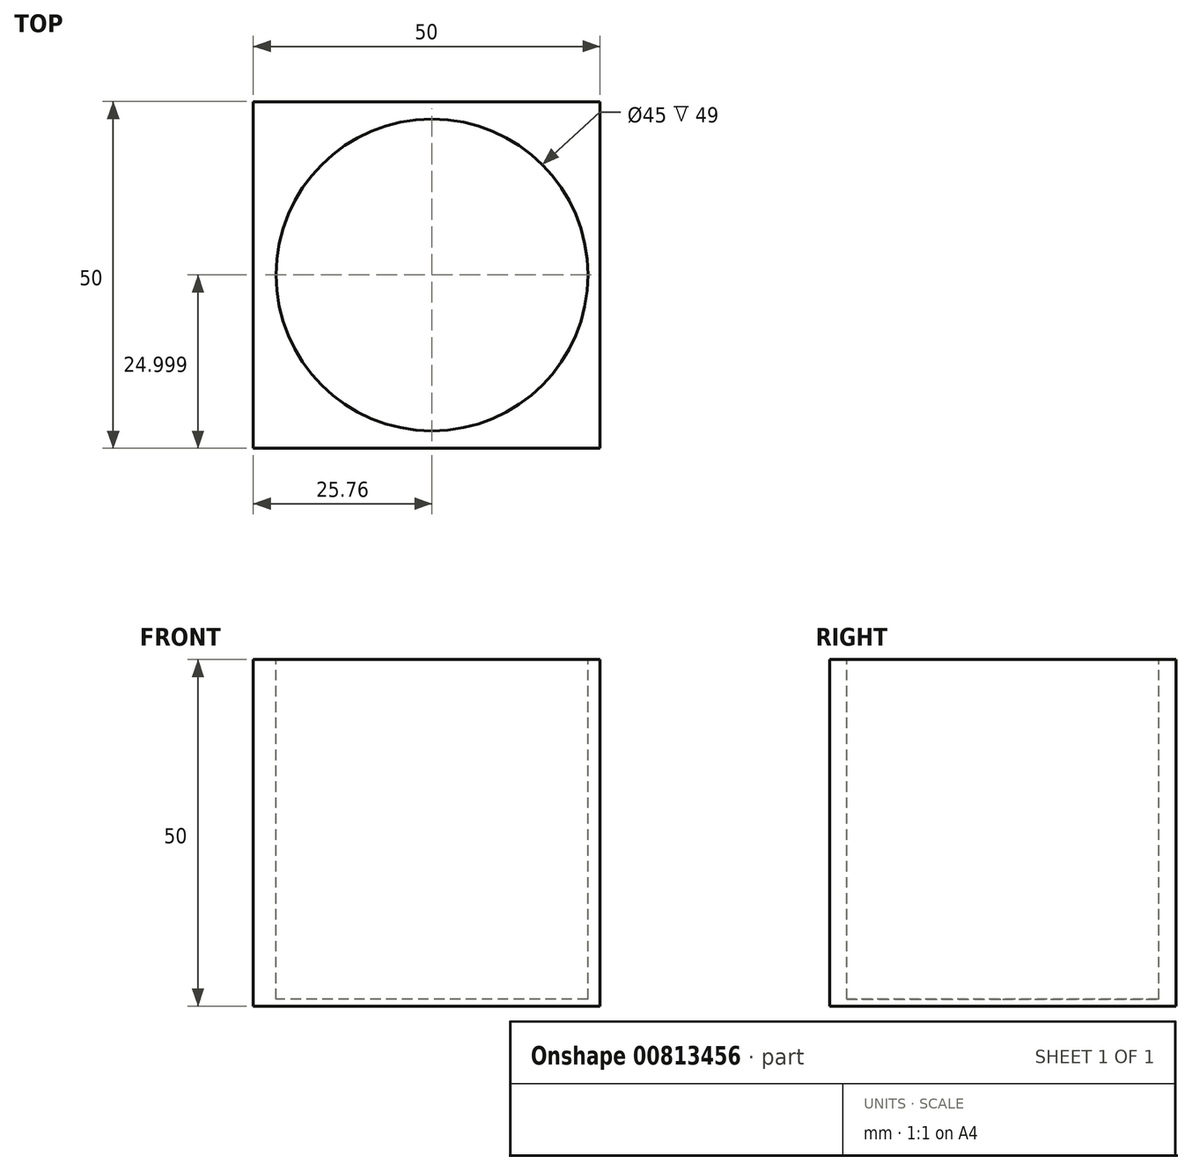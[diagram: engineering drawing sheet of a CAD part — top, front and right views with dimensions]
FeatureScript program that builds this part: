
annotation { "Feature Type Name" : "Feature", "Feature Type Description" : "" }
export const myFeature = defineFeature(function(context is Context, id is Id, definition is map)
    precondition{}
    {
        {
            var Q0;
            Q0=qCreatedBy(makeId("Top.planeOp"),FACE);
            var sketch = newSketch(context, id + "F0", { "sketchPlane" : qUnion([Q0])});
            skLineSegment(sketch, "E0.bottom", {"start": v(-25.76, 30.08) * mm, "end": v(24.24, 30.08) * mm});
            skLineSegment(sketch, "E0.top", {"start": v(-25.76, -19.92) * mm, "end": v(24.24, -19.92) * mm});
            skLineSegment(sketch, "E0.left", {"start": v(-25.76, 30.08) * mm, "end": v(-25.76, -19.92) * mm});
            skLineSegment(sketch, "E0.right", {"start": v(24.24, 30.08) * mm, "end": v(24.24, -19.92) * mm});
            skSolve(sketch);
        }
        {
            var Q0;
            Q0 = qSketchRegion(id + "F0", true);
            extrude(context, id + "F1", {"entities" : qUnion([Q0]), "depth" : 50 * mm, "offsetDistance" : 25 * mm});
        }
        {
            var Q0;
            Q0=makeQuery(id+"F1.opExtrude","CAP_FACE",FACE,{"disambiguationData":[OSD([sQuery(id+"F0.wireOp",EDGE,"E0.bottom"),sQuery(id+"F0.wireOp",EDGE,"E0.top"),sQuery(id+"F0.wireOp",EDGE,"E0.left"),sQuery(id+"F0.wireOp",EDGE,"E0.right")])],"isStart":false});
            var sketch = newSketch(context, id + "F2", { "sketchPlane" : qUnion([Q0])});
            skCircle(sketch, "E1", {"center": v(0, 5.08) * mm, "radius": 22.5 * mm});
            skPoint(sketch, "E1.centerSnap0", {"position": v(-25.76, 5.08) * mm});
            skSolve(sketch);
        }
        {
            var Q0;
            Q0 = qSketchRegion(id + "F2", true);
            extrude(context, id + "F3", {"entities" : qUnion([Q0]), "operationType" : NewBodyOperationType.REMOVE, "oppositeDirection" : true, "depth" : 49 * mm, "offsetDistance" : 25 * mm});
        }
    });
